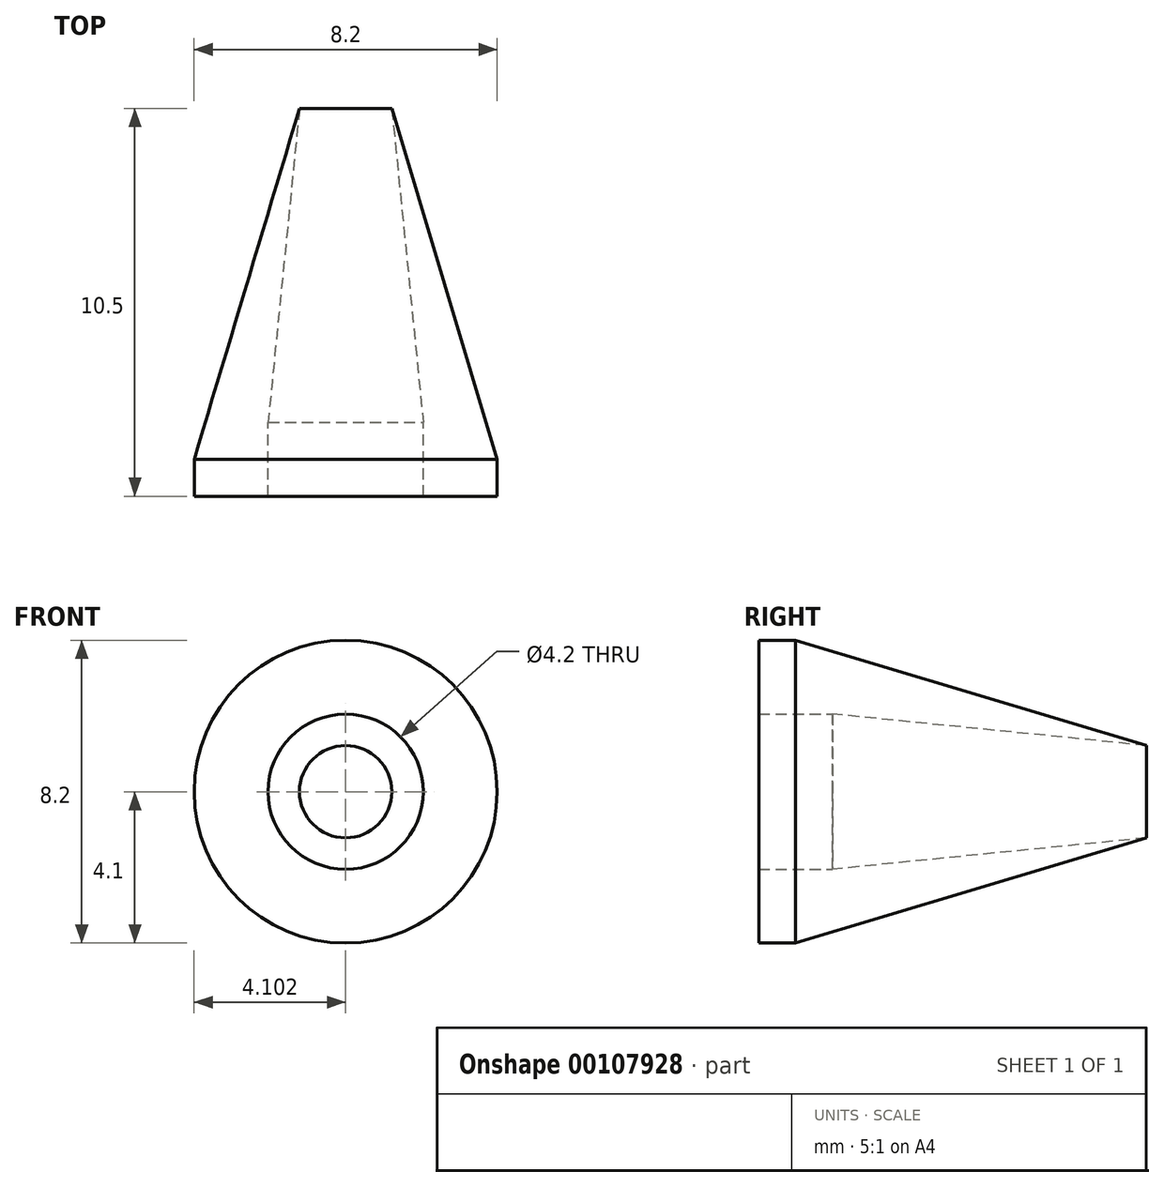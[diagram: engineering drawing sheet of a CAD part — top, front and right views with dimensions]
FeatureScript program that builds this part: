
annotation { "Feature Type Name" : "Feature", "Feature Type Description" : "" }
export const myFeature = defineFeature(function(context is Context, id is Id, definition is map)
    precondition{}
    {
        {
            var Q0;
            Q0=qCreatedBy(makeId("Top.planeOp"),FACE);
            var sketch = newSketch(context, id + "F0", { "sketchPlane" : qUnion([Q0])});
            skLineSegment(sketch, "E0", {"start": v(-30.5, 43.48) * mm, "end": v(-30.5, -9.47) * mm, "construction": true});
            skLineSegment(sketch, "E1", {"start": v(-32.6, 6.65) * mm, "end": v(-34.6, 6.65) * mm});
            skLineSegment(sketch, "E2", {"start": v(-34.6, 6.65) * mm, "end": v(-34.6, 7.65) * mm});
            skLineSegment(sketch, "E3", {"start": v(-31.75, 17.15) * mm, "end": v(-32.6, 8.65) * mm});
            skLineSegment(sketch, "E4", {"start": v(-32.6, 8.65) * mm, "end": v(-32.6, 6.65) * mm});
            skLineSegment(sketch, "E5", {"start": v(-31.75, 17.15) * mm, "end": v(-34.6, 7.65) * mm});
            skSolve(sketch);
        }
        {
            var Q0;
            Q0 = qSketchRegion(id + "F0", true);
            var Q1;
            Q1=sQuery(id+"F0.wireOp",EDGE,"E0");
            revolve(context, id + "F1", {"entities" : qUnion([Q0]), "axis" : qUnion([Q1]), "revolveType" : RevolveType.FULL});
        }
        {
            var Q0;
            Q0=makeQuery(id+"F1.opRevolve","SWEPT_FACE",FACE,{"disambiguationData":[OSD([sQuery(id+"F0.wireOp",EDGE,"E1")])]});
            cPlane(context, id + "F2", {"entities" : qUnion([Q0]), "cplaneType" : CPlaneType.OFFSET, "offset" : 10.5 * mm, "oppositeDirection" : true, "width" : 150 * mm, "height" : 150 * mm});
        }
    });
